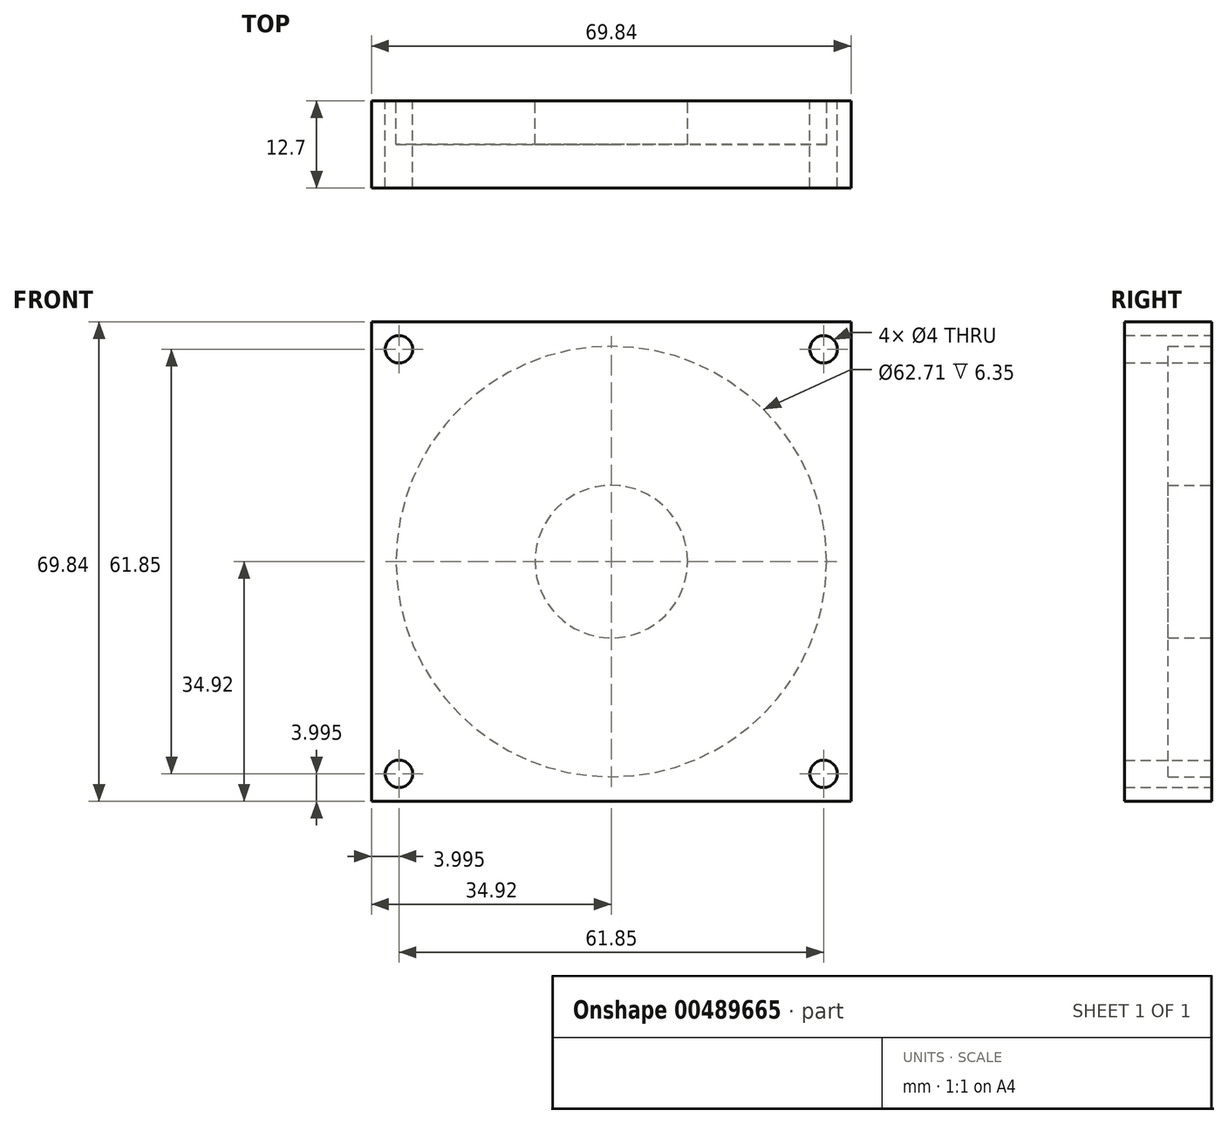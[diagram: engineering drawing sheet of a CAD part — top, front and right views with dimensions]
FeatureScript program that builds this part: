
annotation { "Feature Type Name" : "Feature", "Feature Type Description" : "" }
export const myFeature = defineFeature(function(context is Context, id is Id, definition is map)
    precondition{}
    {
        {
            var Q0;
            Q0=qCreatedBy(makeId("Front.planeOp"),FACE);
            var sketch = newSketch(context, id + "F0", { "sketchPlane" : qUnion([Q0])});
            skLineSegment(sketch, "E0.bottom", {"start": v(34.93, 34.93) * mm, "end": v(-34.93, 34.93) * mm});
            skLineSegment(sketch, "E0.top", {"start": v(34.93, -34.92) * mm, "end": v(-34.93, -34.92) * mm});
            skLineSegment(sketch, "E0.left", {"start": v(34.93, 34.93) * mm, "end": v(34.93, -34.92) * mm});
            skLineSegment(sketch, "E0.right", {"start": v(-34.93, 34.93) * mm, "end": v(-34.93, -34.92) * mm});
            skPoint(sketch, "E0.middle", {"position": v(0, 0) * mm});
            skCircle(sketch, "E1", {"center": v(-30.93, 30.93) * mm, "radius": 2 * mm});
            skCircle(sketch, "E2", {"center": v(30.93, 30.93) * mm, "radius": 2 * mm});
            skCircle(sketch, "E3", {"center": v(30.93, -30.92) * mm, "radius": 2 * mm});
            skCircle(sketch, "E4", {"center": v(-30.93, -30.93) * mm, "radius": 2 * mm});
            skSolve(sketch);
        }
        {
            var Q0;
            Q0=qCreatedBy(makeId("Front.planeOp"),FACE);
            var sketch = newSketch(context, id + "F1", { "sketchPlane" : qUnion([Q0])});
            skCircle(sketch, "E5", {"center": v(0, 0) * mm, "radius": 31.35 * mm});
            skSolve(sketch);
        }
        {
            var Q0;
            Q0=qCreatedBy(makeId("Front.planeOp"),FACE);
            var sketch = newSketch(context, id + "F2", { "sketchPlane" : qUnion([Q0])});
            skCircle(sketch, "E6", {"center": v(0, 0) * mm, "radius": 11.11 * mm});
            skSolve(sketch);
        }
        {
            var Q0;
            Q0=makeQuery(id+"F0.imprint","IMPRINT",FACE,{"disambiguationData":[TD([[makeQuery(id+"F0.imprint","IMPRINT",EDGE,{"derivedFrom":sQuery(id+"F0.wireOp",EDGE,"E0.bottom")}),1.0]])]});
            extrude(context, id + "F3", {"entities" : qUnion([Q0]), "depth" : 12.7 * mm});
        }
        {
            var Q0;
            Q0=makeQuery(id+"F1.imprint","IMPRINT",FACE,{"disambiguationData":[TD([[makeQuery(id+"F1.imprint","IMPRINT",EDGE,{"derivedFrom":sQuery(id+"F1.wireOp",EDGE,"E5")}),1.0]])]});
            extrude(context, id + "F4", {"entities" : qUnion([Q0]), "operationType" : NewBodyOperationType.REMOVE, "depth" : 6.35 * mm});
        }
        {
            var Q0;
            Q0=makeQuery(id+"F2.imprint","IMPRINT",FACE,{"disambiguationData":[TD([[makeQuery(id+"F2.imprint","IMPRINT",EDGE,{"derivedFrom":sQuery(id+"F2.wireOp",EDGE,"E6")}),1.0]])]});
            extrude(context, id + "F5", {"entities" : qUnion([Q0]), "operationType" : NewBodyOperationType.ADD, "depth" : 6.35 * mm});
        }
    });
